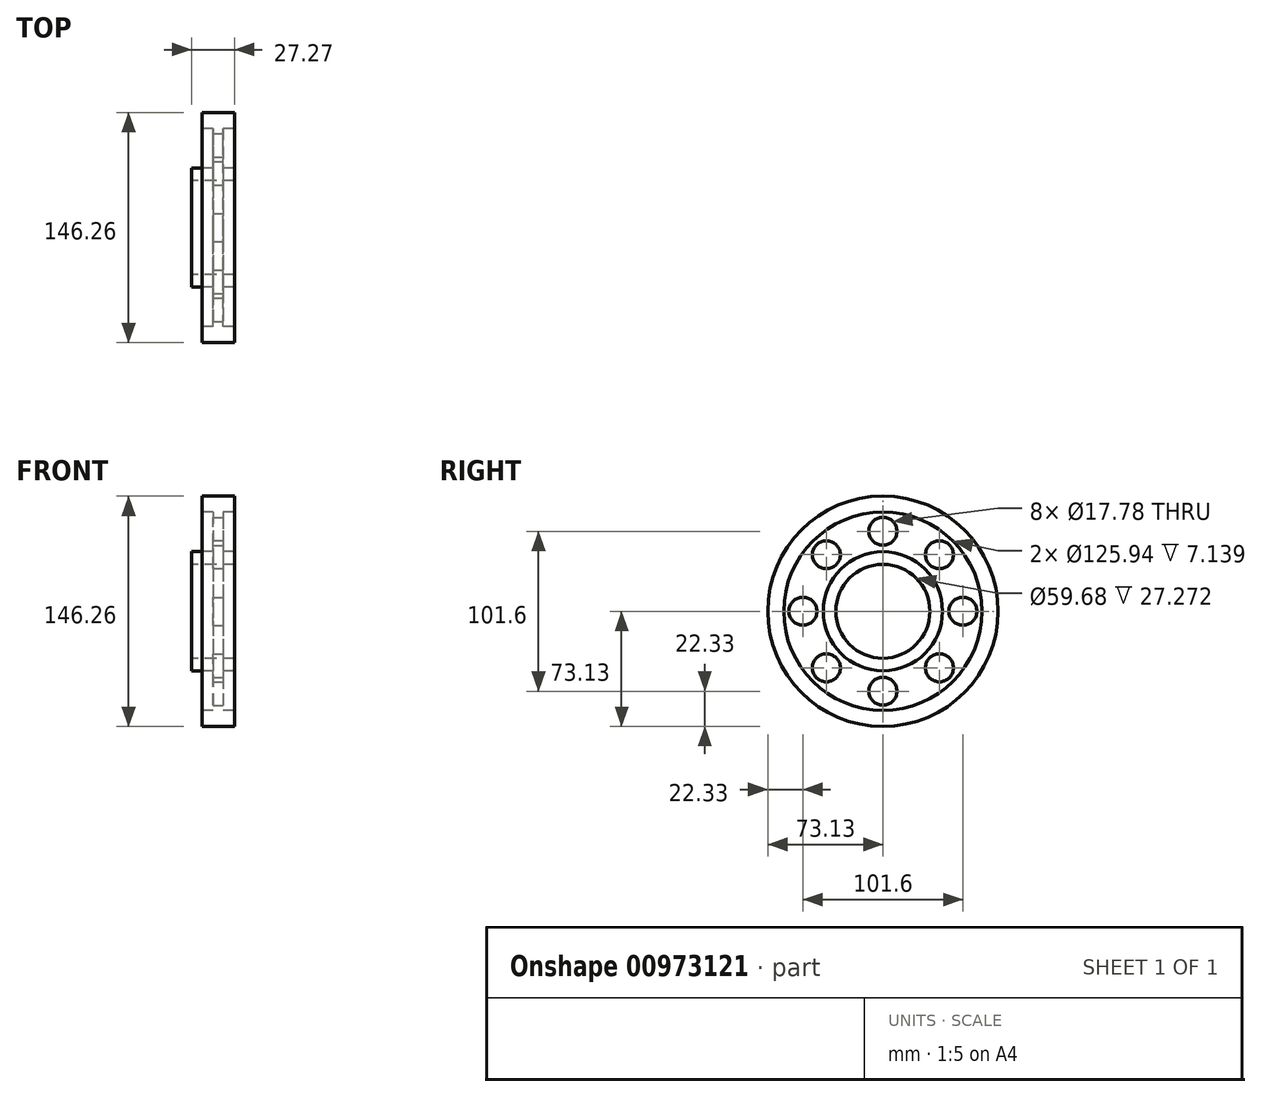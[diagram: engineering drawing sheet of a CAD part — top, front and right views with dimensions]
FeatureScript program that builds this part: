
annotation { "Feature Type Name" : "Feature", "Feature Type Description" : "" }
export const myFeature = defineFeature(function(context is Context, id is Id, definition is map)
    precondition{}
    {
        {
            var Q0;
            Q0=qCreatedBy(makeId("Front.planeOp"),FACE);
            var sketch = newSketch(context, id + "F0", { "sketchPlane" : qUnion([Q0])});
            skLineSegment(sketch, "E0", {"start": v(-117.51, 0) * mm, "end": v(141.5, 0) * mm, "construction": true});
            skLineSegment(sketch, "E1", {"start": v(-20.13, 29.84) * mm, "end": v(7.14, 29.84) * mm});
            skLineSegment(sketch, "E2", {"start": v(7.14, 29.84) * mm, "end": v(7.14, 37.84) * mm});
            skLineSegment(sketch, "E3", {"start": v(7.14, 37.84) * mm, "end": v(0, 37.84) * mm});
            skLineSegment(sketch, "E4", {"start": v(0, 37.84) * mm, "end": v(0, 62.97) * mm});
            skLineSegment(sketch, "E5", {"start": v(0, 62.97) * mm, "end": v(7.14, 62.97) * mm});
            skLineSegment(sketch, "E6", {"start": v(7.14, 62.97) * mm, "end": v(7.14, 73.13) * mm});
            skLineSegment(sketch, "E7", {"start": v(7.14, 73.13) * mm, "end": v(-13.56, 73.13) * mm});
            skLineSegment(sketch, "E8", {"start": v(-13.56, 73.13) * mm, "end": v(-13.56, 62.97) * mm});
            skLineSegment(sketch, "E9", {"start": v(-13.56, 62.97) * mm, "end": v(-6.43, 62.97) * mm});
            skLineSegment(sketch, "E10", {"start": v(-6.43, 62.97) * mm, "end": v(-6.43, 37.84) * mm});
            skLineSegment(sketch, "E11", {"start": v(-6.43, 37.84) * mm, "end": v(-20.13, 37.84) * mm});
            skLineSegment(sketch, "E12", {"start": v(-20.13, 37.84) * mm, "end": v(-20.13, 29.84) * mm});
            skSolve(sketch);
        }
        {
            var Q0;
            Q0=makeQuery(id+"F0.imprint","IMPRINT",FACE,{"disambiguationData":[TD([[makeQuery(id+"F0.imprint","IMPRINT",EDGE,{"derivedFrom":sQuery(id+"F0.wireOp",EDGE,"E1")}),1.0]])]});
            var Q1;
            Q1=sQuery(id+"F0.wireOp",EDGE,"E0");
            revolve(context, id + "F1", {"surfaceOperationType" : NewSurfaceOperationType.NEW, "entities" : qUnion([Q0]), "axis" : qUnion([Q1]), "revolveType" : RevolveType.FULL});
        }
        {
            var Q0;
            Q0=makeQuery(id+"F1.opRevolve","SWEPT_FACE",FACE,{"disambiguationData":[OSD([sQuery(id+"F0.wireOp",EDGE,"E2")])]});
            var sketch = newSketch(context, id + "F2", { "sketchPlane" : qUnion([Q0])});
            skLineSegment(sketch, "E13", {"start": v(0, 0) * mm, "end": v(80.04, 0) * mm, "construction": true});
            skLineSegment(sketch, "E14", {"start": v(0, 0) * mm, "end": v(0, -107.75) * mm});
            skLineSegment(sketch, "E15", {"start": v(0, 0) * mm, "end": v(-79.9, 0) * mm, "construction": true});
            skLineSegment(sketch, "E16", {"start": v(0, 0) * mm, "end": v(0, 93.43) * mm, "construction": true});
            skCircle(sketch, "E17", {"center": v(0, 0) * mm, "radius": 50.8 * mm, "construction": true});
            skCircle(sketch, "E18", {"center": v(50.8, 0) * mm, "radius": 8.9 * mm});
            skCircle(sketch, "E19", {"center": v(0, -50.8) * mm, "radius": 8.9 * mm});
            skCircle(sketch, "E20", {"center": v(-50.8, 0) * mm, "radius": 8.9 * mm});
            skCircle(sketch, "E21", {"center": v(0, 50.8) * mm, "radius": 8.9 * mm});
            skLineSegment(sketch, "E22", {"start": v(0, 0) * mm, "end": v(77.57, 77.57) * mm, "construction": true});
            skCircle(sketch, "E23", {"center": v(35.92, 35.92) * mm, "radius": 8.9 * mm});
            skLineSegment(sketch, "E24", {"start": v(0, 0) * mm, "end": v(57.02, -57.02) * mm, "construction": true});
            skLineSegment(sketch, "E25", {"start": v(0, 0) * mm, "end": v(-58.69, -58.69) * mm, "construction": true});
            skLineSegment(sketch, "E26", {"start": v(0, 0) * mm, "end": v(-58.76, 58.76) * mm, "construction": true});
            skCircle(sketch, "E27", {"center": v(35.92, -35.92) * mm, "radius": 8.9 * mm});
            skCircle(sketch, "E28", {"center": v(-35.92, -35.92) * mm, "radius": 8.9 * mm});
            skCircle(sketch, "E29", {"center": v(-35.92, 35.92) * mm, "radius": 8.9 * mm});
            skSolve(sketch);
        }
        {
            var Q0;
            Q0=makeQuery(id+"F2.imprint","IMPRINT",FACE,{"disambiguationData":[TD([[makeQuery(id+"F2.imprint","IMPRINT",EDGE,{"derivedFrom":sQuery(id+"F2.wireOp",EDGE,"E29")}),1.0]])]});
            var Q1;
            Q1=makeQuery(id+"F2.imprint","IMPRINT",FACE,{"disambiguationData":[TD([[makeQuery(id+"F2.imprint","IMPRINT",EDGE,{"derivedFrom":sQuery(id+"F2.wireOp",EDGE,"E21")}),1.0]])]});
            var Q2;
            Q2=makeQuery(id+"F2.imprint","IMPRINT",FACE,{"disambiguationData":[TD([[makeQuery(id+"F2.imprint","IMPRINT",EDGE,{"derivedFrom":sQuery(id+"F2.wireOp",EDGE,"E23")}),1.0]])]});
            var Q3;
            Q3=makeQuery(id+"F2.imprint","IMPRINT",FACE,{"disambiguationData":[TD([[makeQuery(id+"F2.imprint","IMPRINT",EDGE,{"derivedFrom":sQuery(id+"F2.wireOp",EDGE,"E18")}),1.0]])]});
            var Q4;
            Q4=makeQuery(id+"F2.imprint","IMPRINT",FACE,{"disambiguationData":[TD([[makeQuery(id+"F2.imprint","IMPRINT",EDGE,{"derivedFrom":sQuery(id+"F2.wireOp",EDGE,"E27")}),1.0]])]});
            var Q5;
            {var subQ0=sQuery(id+"F2.wireOp",EDGE,"E19");var subQ1=sQuery(id+"F2.wireOp",EDGE,"E14");var subQ2=makeQuery(id+"F2.imprint","INTERSECT",VERTEX,{"disambiguationData":[OD(0.0)],"derivedFrom":[subQ1,subQ0]});Q5=makeQuery(id+"F2.imprint","IMPRINT",FACE,{"disambiguationData":[TD([[makeQuery(id+"F2.imprint","IMPRINT",EDGE,{"disambiguationData":[TD([[subQ2,1.0]])],"derivedFrom":subQ1}),1.0]])]});}
            var Q6;
            {var subQ0=sQuery(id+"F2.wireOp",EDGE,"E19");var subQ1=sQuery(id+"F2.wireOp",EDGE,"E14");var subQ2=makeQuery(id+"F2.imprint","INTERSECT",VERTEX,{"disambiguationData":[OD(0.0)],"derivedFrom":[subQ1,subQ0]});Q6=makeQuery(id+"F2.imprint","IMPRINT",FACE,{"disambiguationData":[TD([[makeQuery(id+"F2.imprint","IMPRINT",EDGE,{"disambiguationData":[TD([[subQ2,1.0]])],"derivedFrom":subQ1}),-1.0]])]});}
            var Q7;
            Q7=makeQuery(id+"F2.imprint","IMPRINT",FACE,{"disambiguationData":[TD([[makeQuery(id+"F2.imprint","IMPRINT",EDGE,{"derivedFrom":sQuery(id+"F2.wireOp",EDGE,"E28")}),1.0]])]});
            var Q8;
            Q8=makeQuery(id+"F2.imprint","IMPRINT",FACE,{"disambiguationData":[TD([[makeQuery(id+"F2.imprint","IMPRINT",EDGE,{"derivedFrom":sQuery(id+"F2.wireOp",EDGE,"E20")}),1.0]])]});
            extrude(context, id + "F3", {"entities" : qUnion([Q0, Q1, Q2, Q3, Q4, Q5, Q6, Q7, Q8]), "operationType" : NewBodyOperationType.REMOVE, "endBound" : BoundingType.THROUGH_ALL, "oppositeDirection" : true, "depth" : 25.4 * mm, "offsetDistance" : 25.4 * mm});
        }
    });
